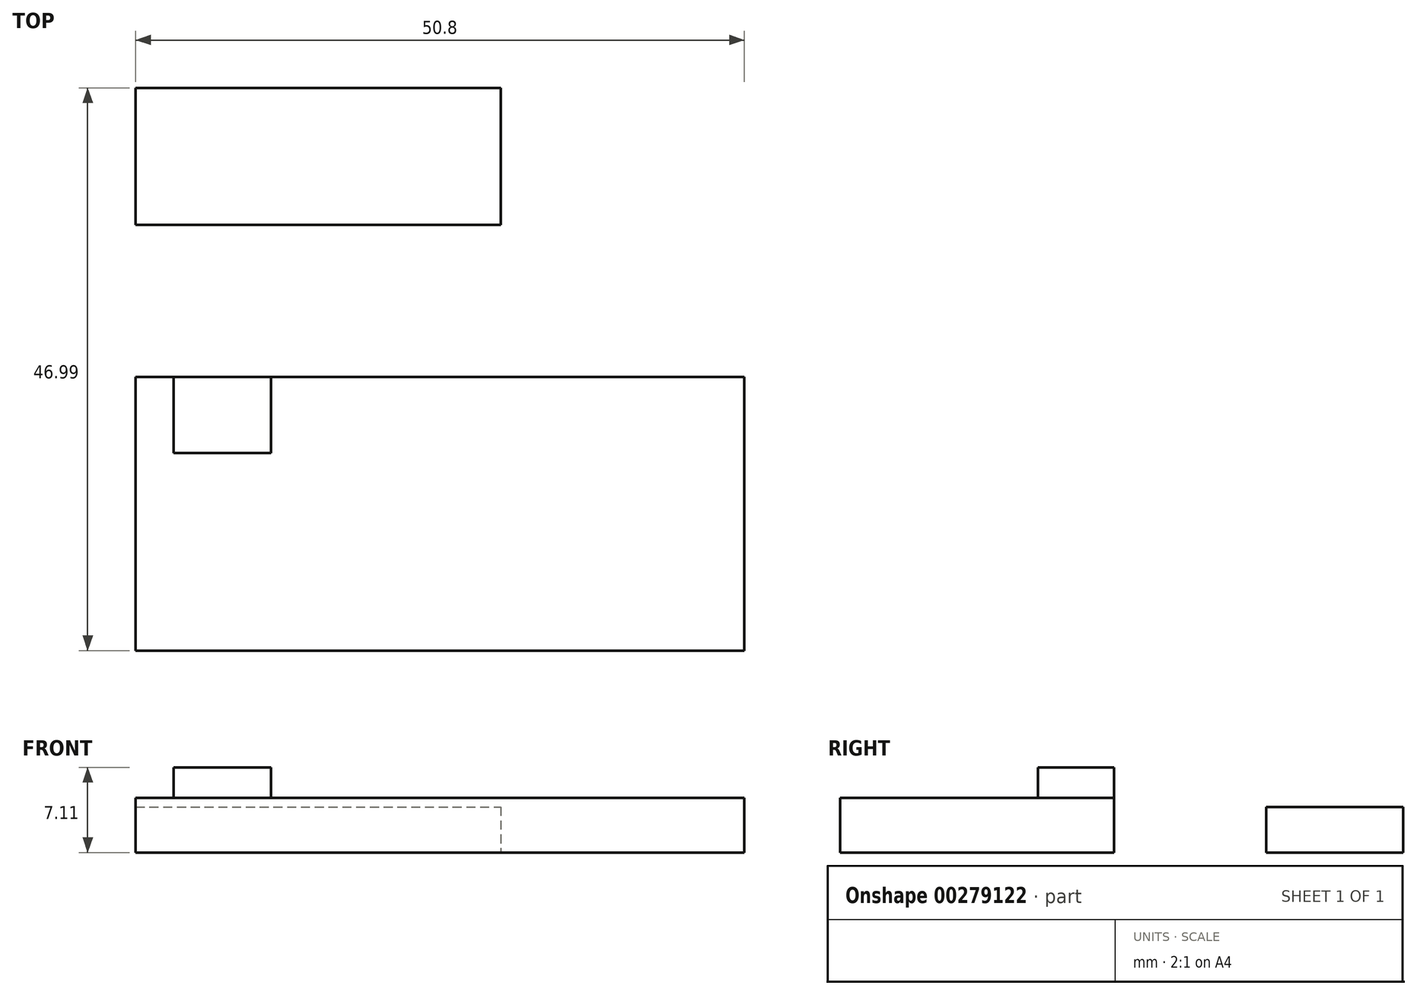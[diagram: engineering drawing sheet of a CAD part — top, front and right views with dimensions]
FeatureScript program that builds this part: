
annotation { "Feature Type Name" : "Feature", "Feature Type Description" : "" }
export const myFeature = defineFeature(function(context is Context, id is Id, definition is map)
    precondition{}
    {
        {
            var Q0;
            Q0=qCreatedBy(makeId("Top.planeOp"),FACE);
            var sketch = newSketch(context, id + "F0", { "sketchPlane" : qUnion([Q0])});
            skLineSegment(sketch, "E0.bottom", {"start": v(-25.4, 0) * mm, "end": v(25.4, 0) * mm});
            skLineSegment(sketch, "E0.top", {"start": v(-25.4, -22.86) * mm, "end": v(25.4, -22.86) * mm});
            skLineSegment(sketch, "E0.left", {"start": v(-25.4, 0) * mm, "end": v(-25.4, -22.86) * mm});
            skLineSegment(sketch, "E0.right", {"start": v(25.4, 0) * mm, "end": v(25.4, -22.86) * mm});
            skSolve(sketch);
        }
        {
            var Q0;
            Q0 = qSketchRegion(id + "F0", true);
            extrude(context, id + "F1", {"entities" : qUnion([Q0]), "depth" : 7.11 * mm});
        }
        {
            var Q0;
            Q0=makeQuery(id+"F1.opExtrude","CAP_FACE",FACE,{"disambiguationData":[OSD([sQuery(id+"F0.wireOp",EDGE,"E0.bottom"),sQuery(id+"F0.wireOp",EDGE,"E0.top"),sQuery(id+"F0.wireOp",EDGE,"E0.left"),sQuery(id+"F0.wireOp",EDGE,"E0.right")])],"isStart":false});
            var sketch = newSketch(context, id + "F2", { "sketchPlane" : qUnion([Q0])});
            skLineSegment(sketch, "E1.bottom", {"start": v(-22.22, 0) * mm, "end": v(-14.1, 0) * mm});
            skLineSegment(sketch, "E1.top", {"start": v(-22.22, -6.35) * mm, "end": v(-14.1, -6.35) * mm});
            skLineSegment(sketch, "E1.left", {"start": v(-22.22, 0) * mm, "end": v(-22.22, -6.35) * mm});
            skLineSegment(sketch, "E1.right", {"start": v(-14.1, 0) * mm, "end": v(-14.1, -6.35) * mm});
            skSolve(sketch);
        }
        {
            var Q0;
            Q0=qCreatedBy(makeId("Top.planeOp"),FACE);
            var sketch = newSketch(context, id + "F3", { "sketchPlane" : qUnion([Q0])});
            skLineSegment(sketch, "E2.bottom", {"start": v(-31.75, -31.75) * mm, "end": v(31.75, -31.75) * mm});
            skLineSegment(sketch, "E2.top", {"start": v(-31.75, 31.75) * mm, "end": v(31.75, 31.75) * mm});
            skLineSegment(sketch, "E2.left", {"start": v(-31.75, -31.75) * mm, "end": v(-31.75, 31.75) * mm});
            skLineSegment(sketch, "E2.right", {"start": v(31.75, -31.75) * mm, "end": v(31.75, 31.75) * mm});
            skSolve(sketch);
        }
        {
            var Q0;
            Q0=makeQuery(id+"F3.imprint","IMPRINT",FACE,{"disambiguationData":[TD([[makeQuery(id+"F3.imprint","IMPRINT",EDGE,{"derivedFrom":sQuery(id+"F3.wireOp",EDGE,"E2.bottom")}),1.0]])]});
            var sketch = newSketch(context, id + "F4", { "sketchPlane" : qUnion([Q0])});
            skLineSegment(sketch, "E3.bottom", {"start": v(-25.4, 24.13) * mm, "end": v(5.08, 24.13) * mm});
            skLineSegment(sketch, "E3.top", {"start": v(-25.4, 12.7) * mm, "end": v(5.08, 12.7) * mm});
            skLineSegment(sketch, "E3.left", {"start": v(-25.4, 24.13) * mm, "end": v(-25.4, 12.7) * mm});
            skLineSegment(sketch, "E3.right", {"start": v(5.08, 24.13) * mm, "end": v(5.08, 12.7) * mm});
            skSolve(sketch);
        }
        {
            var Q0;
            Q0 = qSketchRegion(id + "F4", true);
            extrude(context, id + "F5", {"entities" : qUnion([Q0]), "depth" : 3.8 * mm});
        }
        {
            var Q0;
            Q0=makeQuery(id+"F2.imprint","IMPRINT",FACE,{"disambiguationData":[TD([[makeQuery(id+"F2.imprint","IMPRINT",EDGE,{"derivedFrom":sQuery(id+"F2.wireOp",EDGE,"E1.top")}),-1.0]])]});
            var sketch = newSketch(context, id + "F6", { "sketchPlane" : qUnion([Q0])});
            skText(sketch, "E4", { "text": "Adafruit Feather 32u4 Bluefruit LE", "fontName": "OpenSans-Bold.ttf"});
            const initialGuessF6  = {"E4": [-0.0254, -0.01283, 1, 0, 0.00215]};
            skSetInitialGuess(sketch, initialGuessF6);
            skSolve(sketch);
        }
        {
            var Q0;
            Q0=makeQuery(id+"F2.imprint","IMPRINT",FACE,{"disambiguationData":[TD([[makeQuery(id+"F2.imprint","IMPRINT",EDGE,{"derivedFrom":sQuery(id+"F2.wireOp",EDGE,"E1.top")}),-1.0]])]});
            extrude(context, id + "F7", {"entities" : qUnion([Q0]), "operationType" : NewBodyOperationType.REMOVE, "oppositeDirection" : true, "depth" : 2.54 * mm});
        }
    });
